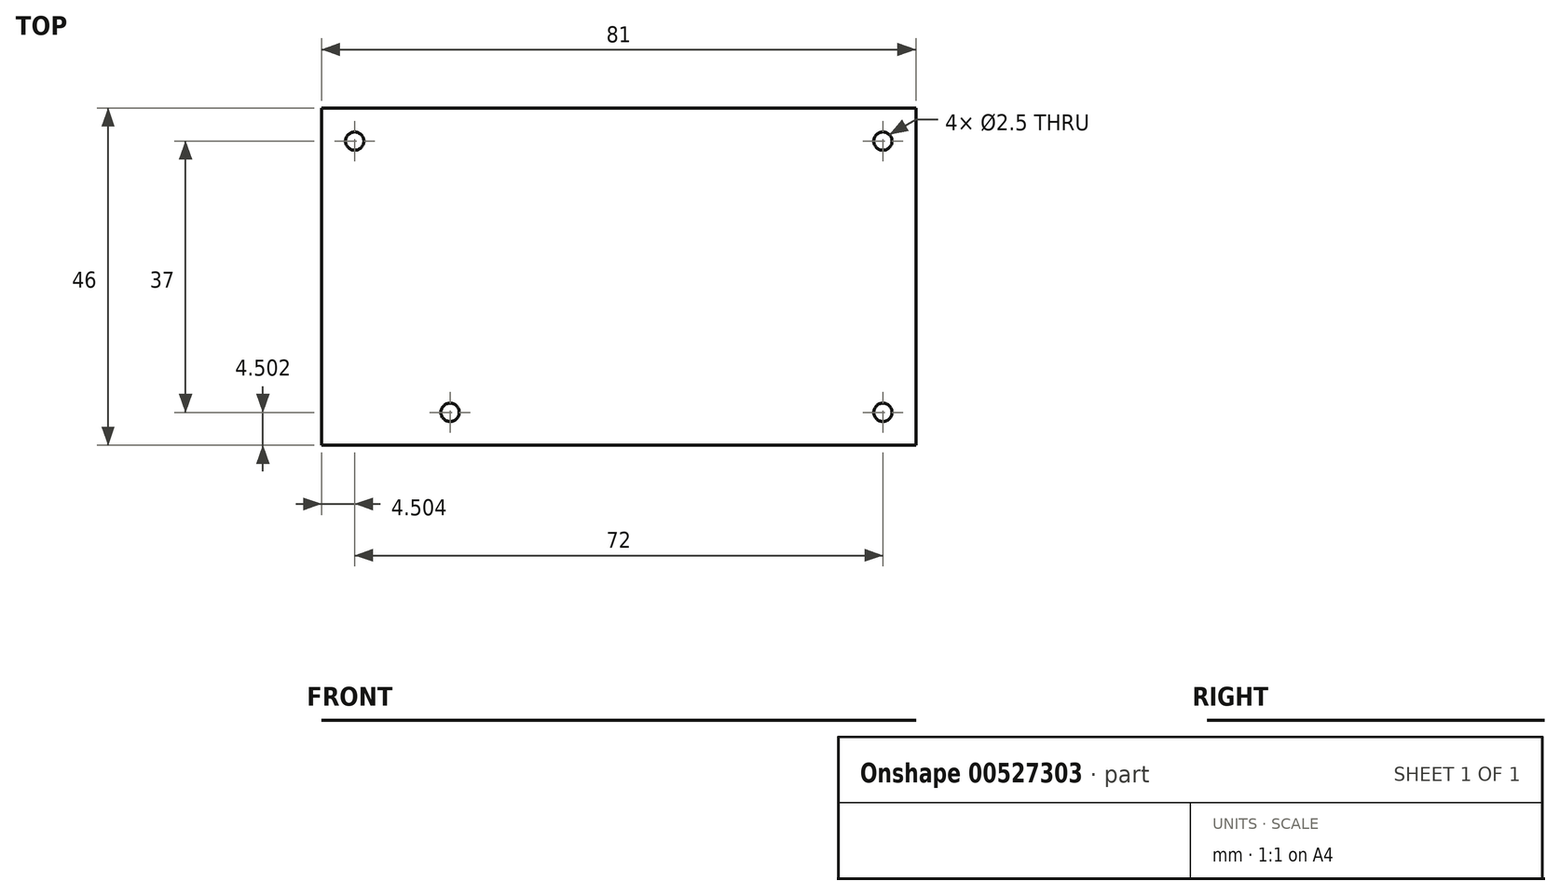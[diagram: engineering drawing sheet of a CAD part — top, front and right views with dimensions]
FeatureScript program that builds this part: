
annotation { "Feature Type Name" : "Feature", "Feature Type Description" : "" }
export const myFeature = defineFeature(function(context is Context, id is Id, definition is map)
    precondition{}
    {
        {
            var Q0;
            Q0=qCreatedBy(makeId("Top.planeOp"),FACE);
            var sketch = newSketch(context, id + "F0", { "sketchPlane" : qUnion([Q0])});
            skLineSegment(sketch, "E0.bottom", {"start": v(-18, 24.81) * mm, "end": v(63, 24.81) * mm});
            skLineSegment(sketch, "E0.top", {"start": v(-18, 15.81) * mm, "end": v(63, 15.81) * mm});
            skLineSegment(sketch, "E0.left", {"start": v(-18, 24.81) * mm, "end": v(-18, 15.81) * mm});
            skLineSegment(sketch, "E0.right", {"start": v(63, 24.81) * mm, "end": v(63, 15.81) * mm});
            skPoint(sketch, "E0.middle", {"position": v(22.5, 20.31) * mm});
            skCircle(sketch, "E1", {"center": v(-13.5, 20.31) * mm, "radius": 1.25 * mm});
            skLineSegment(sketch, "E2", {"start": v(22.5, 20.31) * mm, "end": v(22.5, 15.81) * mm});
            skCircle(sketch, "E3.MirrorC", {"center": v(58.5, 20.31) * mm, "radius": 1.25 * mm});
            skCircle(sketch, "E4", {"center": v(58.5, -16.69) * mm, "radius": 1.25 * mm});
            skCircle(sketch, "E5", {"center": v(-0.5, -16.69) * mm, "radius": 1.25 * mm});
            skLineSegment(sketch, "E6.bottom", {"start": v(-5, -21.19) * mm, "end": v(63, -21.19) * mm});
            skLineSegment(sketch, "E6.top", {"start": v(-5, -12.19) * mm, "end": v(63, -12.19) * mm});
            skLineSegment(sketch, "E6.left", {"start": v(-5, -21.19) * mm, "end": v(-5, -12.19) * mm});
            skLineSegment(sketch, "E6.right", {"start": v(63, -21.19) * mm, "end": v(63, -12.19) * mm});
            skLineSegment(sketch, "E7.bottom", {"start": v(63, 24.81) * mm, "end": v(-18, 24.81) * mm});
            skLineSegment(sketch, "E7.top", {"start": v(63, -21.19) * mm, "end": v(-18, -21.19) * mm});
            skLineSegment(sketch, "E7.left", {"start": v(63, 24.81) * mm, "end": v(63, -21.19) * mm});
            skLineSegment(sketch, "E7.right", {"start": v(-18, 24.81) * mm, "end": v(-18, -21.19) * mm});
            skSolve(sketch);
        }
        {
            var Q0;
            Q0=makeQuery(id+"F0.imprint","IMPRINT",FACE,{"disambiguationData":[TD([[makeQuery(id+"F0.imprint","IMPRINT",EDGE,{"derivedFrom":sQuery(id+"F0.wireOp",EDGE,"E0.bottom")}),-1.0]])]});
            var Q1;
            {var subQ7=sQuery(id+"F0.wireOp",EDGE,"U2NM0KCS-K822-Nf1C-vlmV-AKI8fTmcf5XE.top");Q1=makeQuery(id+"F0.imprint","IMPRINT",FACE,{"disambiguationData":[TD([[makeQuery(id+"F0.imprint","IMPRINT",EDGE,{"derivedFrom":subQ7}),-1.0]])]});}
            var Q2;
            Q2=makeQuery(id+"F0.imprint","IMPRINT",FACE,{"disambiguationData":[TD([[makeQuery(id+"F0.imprint","IMPRINT",EDGE,{"derivedFrom":sQuery(id+"F0.wireOp",EDGE,"4e3c97f5-077a-4da3-b880-ebcf63d0e1af0.MirrorCS")}),-1.0]])]});
            var Q3;
            Q3=makeQuery(id+"F0.imprint","IMPRINT",FACE,{"disambiguationData":[TD([[makeQuery(id+"F0.imprint","IMPRINT",EDGE,{"derivedFrom":sQuery(id+"F0.wireOp",EDGE,"2r6JuJUM-H1xJ-rVk6-LmwX-XtVO87oOarI9.bottom")}),-1.0]])]});
            var Q4;
            {var subQ16=sQuery(id+"F0.wireOp",EDGE,"PUo6MNki-7zzn-Rn6c-szWS-oKsCiA5F92Px.bottom");Q4=makeQuery(id+"F0.imprint","IMPRINT",FACE,{"disambiguationData":[TD([[makeQuery(id+"F0.imprint","IMPRINT",EDGE,{"derivedFrom":subQ16}),1.0]])]});}
            var Q5;
            Q5=makeQuery(id+"F0.imprint","IMPRINT",FACE,{"disambiguationData":[TD([[makeQuery(id+"F0.imprint","IMPRINT",EDGE,{"derivedFrom":sQuery(id+"F0.wireOp",EDGE,"5yf6yUsy-t7qB-Qbny-FLpF-pMkM9fNmBIYO.bottom")}),-1.0]])]});
            var Q6;
            Q6=makeQuery(id+"F0.imprint","IMPRINT",FACE,{"disambiguationData":[TD([[makeQuery(id+"F0.imprint","IMPRINT",EDGE,{"derivedFrom":sQuery(id+"F0.wireOp",EDGE,"3592695a-aeff-4705-9177-f11c87e74c740.MirrorCS")}),-1.0]])]});
            var Q7;
            {var subQ1=sQuery(id+"F0.wireOp",EDGE,"E0.top");var subQ8=makeQuery(id+"F0.imprint","IMPRINT",VERTEX,{"derivedFrom":subQ1});Q7=makeQuery(id+"F0.imprint","IMPRINT",FACE,{"disambiguationData":[TD([[makeQuery(id+"F0.imprint","IMPRINT",EDGE,{"disambiguationData":[TD([[subQ8,1.0]])],"derivedFrom":subQ1}),-1.0]])]});}
            var Q8;
            {var subQ0=sQuery(id+"F0.wireOp",EDGE,"1zIilXki-0rrE-mewM-yc4W-awrqwXFVErq0.bottom");var subQ1=sQuery(id+"F0.wireOp",EDGE,"3HW4A10i-IepW-kTfg-yFla-tKNJ5yOtfOkt");var subQ2=makeQuery(id+"F0.imprint","INTERSECT",VERTEX,{"derivedFrom":[subQ1,subQ0]});Q8=makeQuery(id+"F0.imprint","IMPRINT",FACE,{"disambiguationData":[TD([[makeQuery(id+"F0.imprint","IMPRINT",EDGE,{"disambiguationData":[TD([[subQ2,-1.0]])],"derivedFrom":subQ1}),-1.0]])]});}
            var Q9;
            Q9=makeQuery(id+"F0.imprint","IMPRINT",FACE,{"disambiguationData":[TD([[makeQuery(id+"F0.imprint","IMPRINT",EDGE,{"derivedFrom":sQuery(id+"F0.wireOp",EDGE,"ef4f6fd7-b101-49b2-9d93-8d79d9c1be9c0.MirrorC")}),1.0]])]});
            var Q10;
            Q10=makeQuery(id+"F0.imprint","IMPRINT",FACE,{"disambiguationData":[TD([[makeQuery(id+"F0.imprint","IMPRINT",EDGE,{"derivedFrom":sQuery(id+"F0.wireOp",EDGE,"LNEiIDFf-A2mT-8AOw-AQnD-ryaXKdFsubHj")}),-1.0]])]});
            var Q11;
            {var subQ4=sQuery(id+"F0.wireOp",EDGE,"E5");Q11=makeQuery(id+"F0.imprint","IMPRINT",FACE,{"disambiguationData":[TD([[makeQuery(id+"F0.imprint","IMPRINT",EDGE,{"derivedFrom":subQ4}),-1.0]])]});}
            var Q12;
            Q12=makeQuery(id+"F0.imprint","IMPRINT",FACE,{"disambiguationData":[TD([[makeQuery(id+"F0.imprint","IMPRINT",EDGE,{"derivedFrom":sQuery(id+"F0.wireOp",EDGE,"E4")}),-1.0]])]});
            var Q13;
            Q13=makeQuery(id+"F0.imprint","IMPRINT",FACE,{"disambiguationData":[TD([[makeQuery(id+"F0.imprint","IMPRINT",EDGE,{"derivedFrom":sQuery(id+"F0.wireOp",EDGE,"E1")}),-1.0]])]});
            extrude(context, id + "F1", {"entities" : qUnion([Q0, Q1, Q2, Q3, Q4, Q5, Q6, Q7, Q8, Q9, Q10, Q11, Q12, Q13]), "depth" : 1 / 203.2 * mm, "offsetDistance" : 25 * mm});
        }
    });
